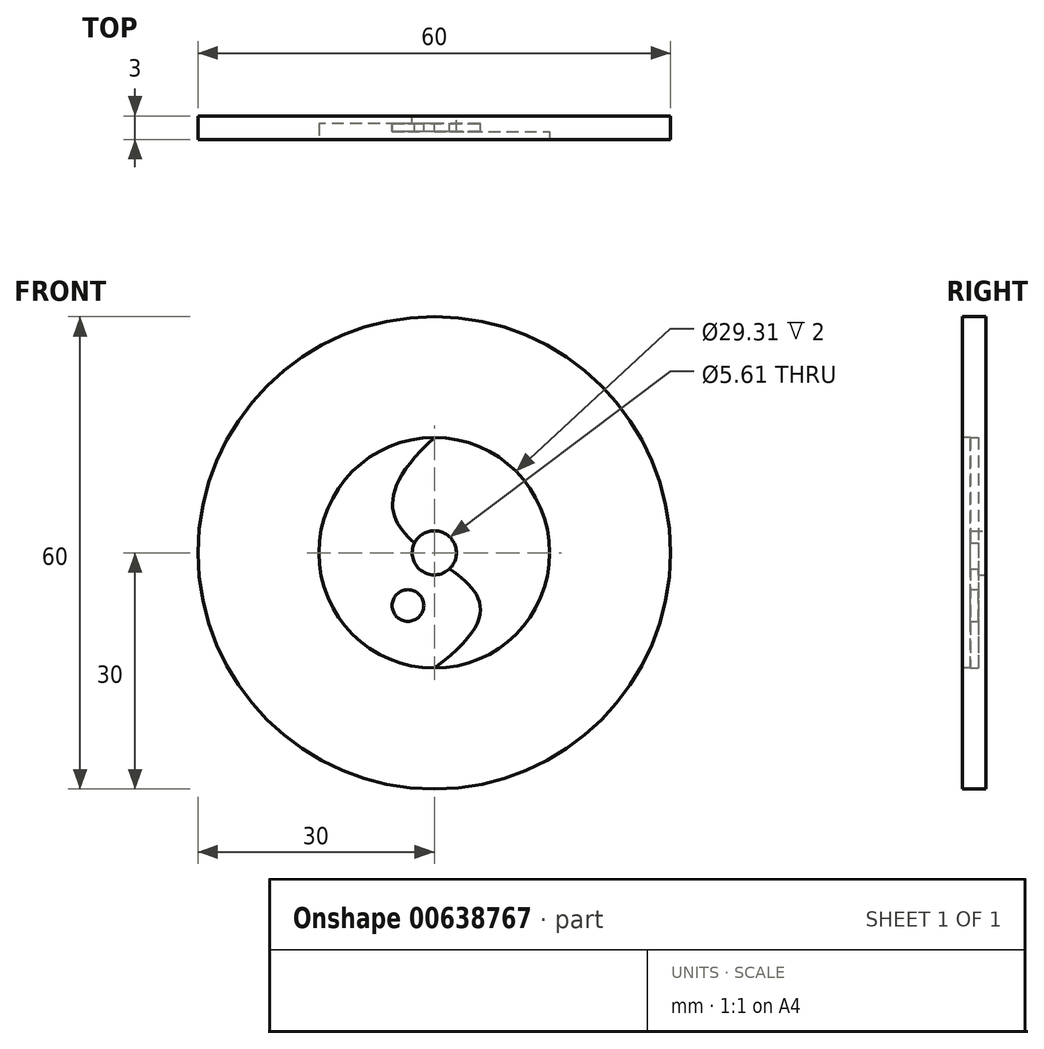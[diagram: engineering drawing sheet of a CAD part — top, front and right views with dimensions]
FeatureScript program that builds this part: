
annotation { "Feature Type Name" : "Feature", "Feature Type Description" : "" }
export const myFeature = defineFeature(function(context is Context, id is Id, definition is map)
    precondition{}
    {
        {
            var Q0;
            Q0=qCreatedBy(makeId("Front.planeOp"),FACE);
            var sketch = newSketch(context, id + "F0", { "sketchPlane" : qUnion([Q0])});
            skCircle(sketch, "E0", {"center": v(0, 0) * mm, "radius": 30 * mm});
            skCircle(sketch, "E1", {"center": v(0, 0) * mm, "radius": 2.8 * mm});
            skSolve(sketch);
        }
        {
            var Q0;
            Q0=makeQuery(id+"F0.imprint","IMPRINT",FACE,{"disambiguationData":[TD([[makeQuery(id+"F0.imprint","IMPRINT",EDGE,{"derivedFrom":sQuery(id+"F0.wireOp",EDGE,"E0")}),1.0]])]});
            extrude(context, id + "F1", {"entities" : qUnion([Q0]), "depth" : 3 * mm, "offsetDistance" : 25 * mm});
        }
        {
            var Q0;
            Q0=makeQuery(id+"F1.opExtrude","CAP_FACE",FACE,{"disambiguationData":[OSD([sQuery(id+"F0.wireOp",EDGE,"E0"),sQuery(id+"F0.wireOp",EDGE,"E1")])],"isStart":false});
            var sketch = newSketch(context, id + "F2", { "sketchPlane" : qUnion([Q0])});
            skCircle(sketch, "E2", {"center": v(0, 0) * mm, "radius": 14.65 * mm});
            skSolve(sketch);
        }
        {
            var Q0;
            Q0=makeQuery(id+"F2.imprint","IMPRINT",FACE,{"disambiguationData":[TD([[makeQuery(id+"F2.imprint","IMPRINT",EDGE,{"derivedFrom":sQuery(id+"F2.wireOp",EDGE,"E2")}),1.0]])]});
            extrude(context, id + "F3", {"entities" : qUnion([Q0]), "operationType" : NewBodyOperationType.REMOVE, "oppositeDirection" : true, "depth" : 2 * mm, "offsetDistance" : 25 * mm});
        }
        {
            var Q0;
            Q0=makeQuery(id+"F3.boolean.opBoolean","COPY",FACE,{"derivedFrom":makeQuery(id+"F3.opExtrude","CAP_FACE",FACE,{"disambiguationData":[OSD([sQuery(id+"F0.wireOp",EDGE,"E1"),sQuery(id+"F2.wireOp",EDGE,"E2")])],"isStart":false})});
            var sketch = newSketch(context, id + "F4", { "sketchPlane" : qUnion([Q0])});
            skFitSpline(sketch, "E3", {"points": [v(0, 14.65) * mm, v(0, -14.65) * mm], "startDerivative": vector(-56.3, -51.57) * mm, "endDerivative": vector(-59.65, -43.96) * mm});
            skSolve(sketch);
        }
        {
            var Q0;
            {var subQ0=sQuery(id+"F4.wireOp",EDGE,"E3");var subQ1=makeQuery(id+"F3.boolean.opBoolean","COPY",EDGE,{"derivedFrom":makeQuery(id+"F3.opExtrude","CAP_EDGE",EDGE,{"disambiguationData":[OSD([sQuery(id+"F2.wireOp",EDGE,"E2")])],"isStart":false})});var subQ2=makeQuery(id+"F4.imprint","INTERSECT",VERTEX,{"disambiguationData":[OD(0.0)],"derivedFrom":[subQ1,subQ0]});Q0=makeQuery(id+"F4.imprint","IMPRINT",FACE,{"disambiguationData":[TD([[makeQuery(id+"F4.imprint","IMPRINT",EDGE,{"disambiguationData":[TD([[subQ2,-1.0]])],"derivedFrom":subQ0}),1.0]])]});}
            extrude(context, id + "F5", {"entities" : qUnion([Q0]), "operationType" : NewBodyOperationType.ADD, "depth" : 1 * mm, "offsetDistance" : 25 * mm});
        }
        {
            var Q0;
            Q0=makeQuery(id+"F3.boolean.opBoolean","COPY",FACE,{"derivedFrom":makeQuery(id+"F3.opExtrude","CAP_FACE",FACE,{"disambiguationData":[OSD([sQuery(id+"F0.wireOp",EDGE,"E1"),sQuery(id+"F2.wireOp",EDGE,"E2")])],"isStart":false})});
            var sketch = newSketch(context, id + "F6", { "sketchPlane" : qUnion([Q0])});
            skCircle(sketch, "E4", {"center": v(3.99, 7.81) * mm, "radius": 2.01 * mm});
            skCircle(sketch, "E5", {"center": v(-3.35, -6.7) * mm, "radius": 2.01 * mm});
            skFitSpline(sketch, "E6", {"points": [v(-29.83, 3.55) * mm, v(-12.88, 27.19) * mm], "startDerivative": vector(35.6, 14) * mm, "endDerivative": vector(2.13, 35) * mm});
            skFitSpline(sketch, "E7", {"points": [v(-12.88, 27.19) * mm, v(19.17, 23.03) * mm], "startDerivative": vector(38.65, -29.52) * mm, "endDerivative": vector(32.87, 10.35) * mm});
            skFitSpline(sketch, "E8", {"points": [v(19.17, 23.03) * mm, v(29.62, -4.06) * mm], "startDerivative": vector(-12.78, -36.52) * mm, "endDerivative": vector(23.13, -12.18) * mm});
            skFitSpline(sketch, "E9", {"points": [v(29.62, -4.06) * mm, v(12.88, -27.09) * mm], "startDerivative": vector(-40.78, -15.52) * mm, "endDerivative": vector(4.57, -29.83) * mm});
            skFitSpline(sketch, "E10", {"points": [v(12.88, -27.09) * mm, v(-21, -21.2) * mm], "startDerivative": vector(-36.22, 26.78) * mm, "endDerivative": vector(-34.4, -7.3) * mm});
            skFitSpline(sketch, "E11", {"points": [v(-29.83, 3.55) * mm, v(-21, -21.2) * mm], "startDerivative": vector(30.43, -14) * mm, "endDerivative": vector(-7.6, -35.3) * mm});
            skSolve(sketch);
        }
        {
            var Q0;
            Q0=makeQuery(id+"F6.imprint","IMPRINT",FACE,{"disambiguationData":[TD([[makeQuery(id+"F6.imprint","IMPRINT",EDGE,{"derivedFrom":sQuery(id+"F6.wireOp",EDGE,"E5")}),1.0]])]});
            extrude(context, id + "F7", {"entities" : qUnion([Q0]), "operationType" : NewBodyOperationType.ADD, "depth" : 1 * mm, "offsetDistance" : 25 * mm});
        }
        {
            var Q0;
            Q0=sQuery(id+"F6.wireOp",EDGE,"E4");
            extrude(context, id + "F8", {"bodyType" : ToolBodyType.SURFACE, "surfaceEntities" : qUnion([Q0]), "depth" : -1 * mm, "offsetDistance" : 25 * mm});
        }
        {
            var Q0;
            Q0=sQuery(id+"F6.wireOp",EDGE,"E7");
            var Q1;
            Q1=sQuery(id+"F6.wireOp",EDGE,"E6");
            var Q2;
            Q2=sQuery(id+"F6.wireOp",EDGE,"E11");
            var Q3;
            Q3=sQuery(id+"F6.wireOp",EDGE,"E10");
            var Q4;
            Q4=sQuery(id+"F6.wireOp",EDGE,"E9");
            var Q5;
            Q5=sQuery(id+"F6.wireOp",EDGE,"E8");
            extrude(context, id + "F9", {"bodyType" : ToolBodyType.SURFACE, "surfaceEntities" : qUnion([Q0, Q1, Q2, Q3, Q4, Q5]), "depth" : -2 * mm, "offsetDistance" : 25 * mm});
        }
        {
            var Q0;
            Q0=sQuery(id+"F6.wireOp",EDGE,"E4");
            extrude(context, id + "F10", {"bodyType" : ToolBodyType.SURFACE, "surfaceEntities" : qUnion([Q0]), "depth" : -1 * mm, "offsetDistance" : 25 * mm});
        }
    });
